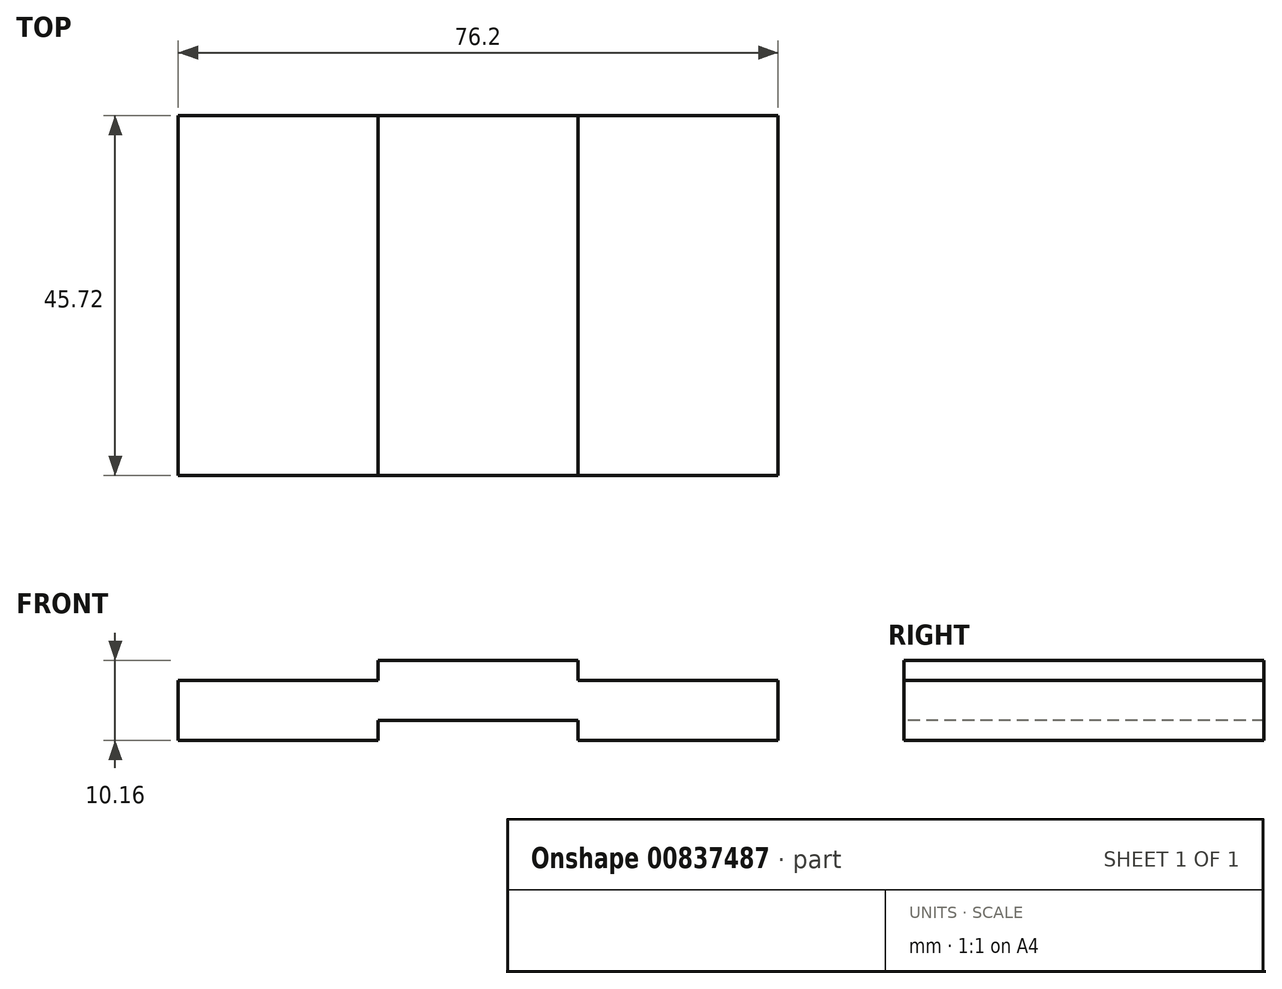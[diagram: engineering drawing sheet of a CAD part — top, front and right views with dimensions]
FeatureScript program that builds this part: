
annotation { "Feature Type Name" : "Feature", "Feature Type Description" : "" }
export const myFeature = defineFeature(function(context is Context, id is Id, definition is map)
    precondition{}
    {
        {
            var Q0;
            Q0=qCreatedBy(makeId("Front.planeOp"),FACE);
            var sketch = newSketch(context, id + "F0", { "sketchPlane" : qUnion([Q0])});
            skLineSegment(sketch, "E0", {"start": v(0, 0) * mm, "end": v(-38.1, 0) * mm});
            skLineSegment(sketch, "E1.MirrorCS", {"start": v(0, 0) * mm, "end": v(38.1, 0) * mm});
            skLineSegment(sketch, "E2", {"start": v(-38.1, 0) * mm, "end": v(-38.1, 7.62) * mm});
            skLineSegment(sketch, "E3", {"start": v(-38.1, 7.62) * mm, "end": v(38.1, 7.62) * mm});
            skLineSegment(sketch, "E4", {"start": v(38.1, 7.62) * mm, "end": v(38.1, 0) * mm});
            skSolve(sketch);
        }
        {
            var Q0;
            Q0=makeQuery(id+"F0.imprint","IMPRINT",FACE,{"disambiguationData":[TD([[makeQuery(id+"F0.imprint","IMPRINT",EDGE,{"derivedFrom":sQuery(id+"F0.wireOp",EDGE,"E0")}),-1.0]])]});
            extrude(context, id + "F1", {"entities" : qUnion([Q0]), "oppositeDirection" : true, "depth" : 45.72 * mm, "offsetDistance" : 25.4 * mm});
        }
        {
            var Q0;
            Q0=makeQuery(id+"F1.opExtrude","CAP_FACE",FACE,{"disambiguationData":[OSD([sQuery(id+"F0.wireOp",EDGE,"E0"),sQuery(id+"F0.wireOp",EDGE,"E1.MirrorCS"),sQuery(id+"F0.wireOp",EDGE,"E2"),sQuery(id+"F0.wireOp",EDGE,"E3"),sQuery(id+"F0.wireOp",EDGE,"E4")])],"isStart":true});
            cPlane(context, id + "F2", {"entities" : qUnion([Q0]), "cplaneType" : CPlaneType.OFFSET, "offset" : 0 * mm, "width" : 152.4 * mm, "height" : 152.4 * mm});
        }
        {
            var Q0;
            Q0=qCreatedBy(id+"F2.planeOp",FACE);
            var sketch = newSketch(context, id + "F3", { "sketchPlane" : qUnion([Q0])});
            skLineSegment(sketch, "E5", {"start": v(0, 0) * mm, "end": v(-12.7, 0) * mm});
            skLineSegment(sketch, "E6.MirrorCS", {"start": v(0, 0) * mm, "end": v(12.7, 0) * mm});
            skLineSegment(sketch, "E7", {"start": v(-12.7, 0) * mm, "end": v(-12.7, 2.54) * mm});
            skLineSegment(sketch, "E8", {"start": v(-12.7, 2.54) * mm, "end": v(12.7, 2.54) * mm});
            skLineSegment(sketch, "E9", {"start": v(12.7, 2.54) * mm, "end": v(12.7, 0) * mm});
            skSolve(sketch);
        }
        {
            var Q0;
            Q0=makeQuery(id+"F3.imprint","IMPRINT",FACE,{"disambiguationData":[TD([[makeQuery(id+"F3.imprint","IMPRINT",EDGE,{"derivedFrom":sQuery(id+"F3.wireOp",EDGE,"E5")}),-1.0]])]});
            extrude(context, id + "F4", {"entities" : qUnion([Q0]), "operationType" : NewBodyOperationType.REMOVE, "endBound" : BoundingType.THROUGH_ALL, "oppositeDirection" : true, "depth" : 25.4 * mm, "offsetDistance" : 25.4 * mm});
        }
        {
            var Q0;
            Q0=qCreatedBy(id+"F2.planeOp",FACE);
            cPlane(context, id + "F5", {"entities" : qUnion([Q0]), "cplaneType" : CPlaneType.OFFSET, "offset" : 0 * mm, "width" : 152.4 * mm, "height" : 152.4 * mm});
        }
        {
            var Q0;
            Q0=qCreatedBy(id+"F5.planeOp",FACE);
            var sketch = newSketch(context, id + "F6", { "sketchPlane" : qUnion([Q0])});
            skLineSegment(sketch, "E10", {"start": v(0, 7.62) * mm, "end": v(-12.7, 7.62) * mm});
            skLineSegment(sketch, "E11.MirrorCS", {"start": v(0, 7.62) * mm, "end": v(12.7, 7.62) * mm});
            skLineSegment(sketch, "E12", {"start": v(-12.7, 7.62) * mm, "end": v(-12.7, 10.16) * mm});
            skLineSegment(sketch, "E13", {"start": v(-12.7, 10.16) * mm, "end": v(12.7, 10.16) * mm});
            skLineSegment(sketch, "E14", {"start": v(12.7, 10.16) * mm, "end": v(12.7, 7.62) * mm});
            skSolve(sketch);
        }
        {
            var Q0;
            Q0=makeQuery(id+"F6.imprint","IMPRINT",FACE,{"disambiguationData":[TD([[makeQuery(id+"F6.imprint","IMPRINT",EDGE,{"derivedFrom":sQuery(id+"F6.wireOp",EDGE,"E10")}),-1.0]])]});
            extrude(context, id + "F7", {"entities" : qUnion([Q0]), "operationType" : NewBodyOperationType.ADD, "oppositeDirection" : true, "depth" : 45.72 * mm, "offsetDistance" : 25.4 * mm});
        }
    });
